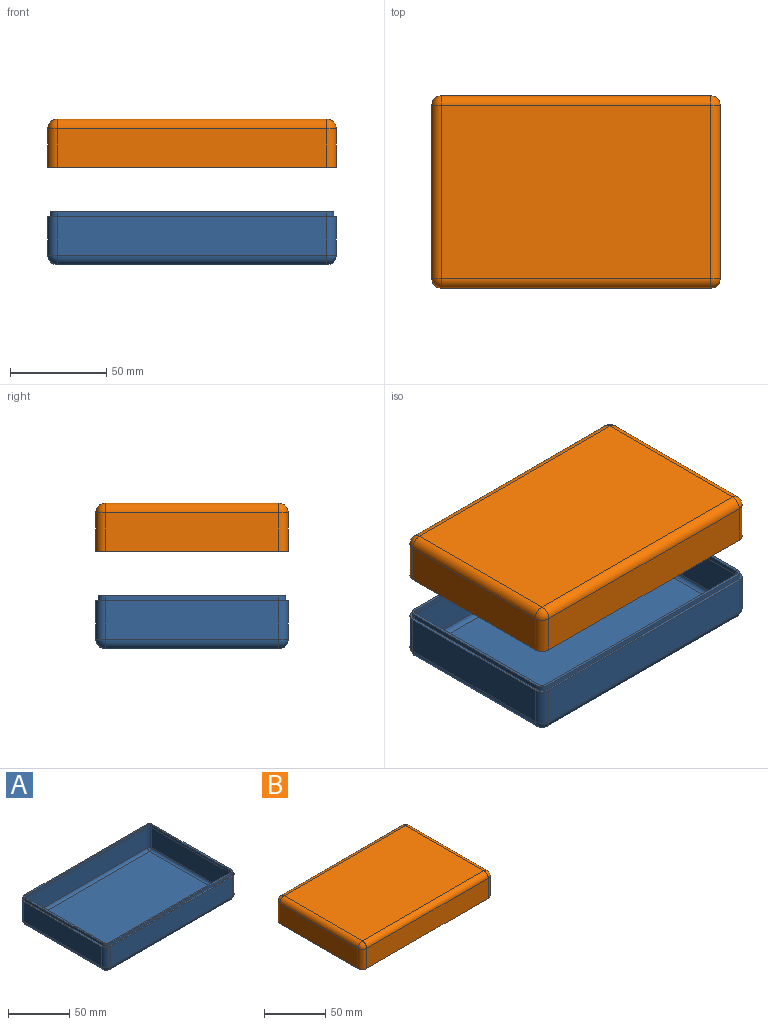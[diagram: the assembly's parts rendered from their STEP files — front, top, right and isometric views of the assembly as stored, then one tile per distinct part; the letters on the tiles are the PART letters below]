
ASSEMBLY  parts=2 mates=1
PART A: 53 faces, bbox 150x100x27.5 mm
  f0: plane 150x100mm, normal (0,0,1), area 624.4mm2, adj f10,f11,f12,f13,f14,f15,f16,f17
  f1: plane 140x90mm, normal (0,0,-1), area 12600mm2, adj f2,f3,f4,f5
  f2: cylinder r=5mm len=140mm, axis (1,0,0), area 1099.6mm2, adj f1,f8,f9,f17
  f3: cylinder r=5mm len=90mm, axis (0,1,0), area 706.9mm2, adj f1,f7,f9,f16
  f4: cylinder r=5mm len=140mm, axis (-1,0,0), area 1099.6mm2, adj f1,f6,f7,f14
  f5: cylinder r=5mm len=90mm, axis (0,-1,0), area 706.9mm2, adj f1,f6,f8,f12
  f6: sphere r=5mm, area 39.3mm2, adj f4,f5,f10
  f7: sphere r=5mm, area 39.3mm2, adj f3,f4,f13
  f8: sphere r=5mm, area 39.3mm2, adj f2,f5,f11
  f9: sphere r=5mm, area 39.3mm2, adj f2,f3,f15
  f10: cylinder r=5mm len=20mm, axis (0,0,1), area 157.1mm2, adj f0,f6,f12,f14
  f11: cylinder r=5mm len=20mm, axis (0,0,-1), area 157.1mm2, adj f0,f8,f12,f17
  f12: plane 90x20mm, normal (-1,0,0), area 1800mm2, adj f0,f5,f10,f11
  f13: cylinder r=5mm len=20mm, axis (0,0,-1), area 157.1mm2, adj f0,f7,f14,f16
  f14: plane 140x20mm, normal (0,1,0), area 2800mm2, adj f0,f4,f10,f13
  f15: cylinder r=5mm len=20mm, axis (0,0,1), area 157.1mm2, adj f0,f9,f16,f17
  f16: plane 90x20mm, normal (1,0,0), area 1800mm2, adj f0,f3,f13,f15
  f17: plane 140x20mm, normal (0,-1,0), area 2800mm2, adj f0,f2,f11,f15
  f18: cylinder r=3.72mm len=3.72mm, axis (0,0,-1), area 14.6mm2, adj f0,f20,f32,f33
  f19: cylinder r=2.47mm len=2.5mm, axis (0,0,-1), area 9.7mm2, adj f21,f32,f34,f35
  f20: plane 90x2.5mm, normal (-1,0,0), area 225mm2, adj f0,f18,f22,f32
  f21: plane 90x2.5mm, normal (1,0,0), area 225mm2, adj f19,f23,f32,f34
  f22: cylinder r=3.72mm len=3.72mm, axis (0,0,-1), area 14.6mm2, adj f0,f20,f24,f32
  f23: cylinder r=2.47mm len=2.5mm, axis (0,0,-1), area 9.7mm2, adj f21,f25,f32,f34
  f24: plane 140x2.5mm, normal (0,-1,0), area 350mm2, adj f0,f22,f26,f32
  f25: plane 140x2.5mm, normal (0,1,0), area 350mm2, adj f23,f27,f32,f34
  f26: cylinder r=3.72mm len=3.72mm, axis (0,0,-1), area 14.6mm2, adj f0,f24,f28,f32
  f27: cylinder r=2.47mm len=2.5mm, axis (0,0,-1), area 9.7mm2, adj f25,f29,f32,f34
  f28: plane 90x2.5mm, normal (1,0,0), area 225mm2, adj f0,f26,f30,f32
  f29: plane 90x2.5mm, normal (-1,0,0), area 225mm2, adj f27,f31,f32,f34
  f30: cylinder r=3.72mm len=3.72mm, axis (0,0,-1), area 14.6mm2, adj f0,f28,f32,f33
  f31: cylinder r=2.47mm len=2.5mm, axis (0,0,-1), area 9.7mm2, adj f29,f32,f34,f35
  f32: plane 147.44x97.44mm, normal (0,0,1), area 599.3mm2, adj f18,f19,f20,f21,f22,f23,f24,f25
  f33: plane 140x2.5mm, normal (0,1,0), area 350mm2, adj f0,f18,f30,f32
  f34: plane 145x95mm, normal (0,0,-1), area 14.8mm2, adj f19,f21,f23,f25,f27,f29,f31,f35
  f35: plane 140x2.5mm, normal (0,-1,0), area 350mm2, adj f19,f31,f32,f34
  f36: plane 140x90mm, normal (0,0,1), area 12600mm2, adj f37,f39,f41,f43
  f37: cylinder r=2.5mm len=90mm, axis (0,-1,0), area 353.4mm2, adj f36,f38,f44,f52
  f38: sphere r=2.5mm, area 9.8mm2, adj f37,f39,f51
  f39: cylinder r=2.5mm len=140mm, axis (-1,0,0), area 549.8mm2, adj f36,f38,f40,f50
  f40: sphere r=2.5mm, area 9.8mm2, adj f39,f41,f49
  f41: cylinder r=2.5mm len=90mm, axis (0,1,0), area 353.4mm2, adj f36,f40,f42,f48
  f42: sphere r=2.5mm, area 9.8mm2, adj f41,f43,f47
  f43: cylinder r=2.5mm len=140mm, axis (1,0,0), area 549.8mm2, adj f36,f42,f44,f46
  f44: sphere r=2.5mm, area 9.8mm2, adj f37,f43,f45
  f45: cylinder r=2.5mm len=20mm, axis (0,0,-1), area 78.5mm2, adj f34,f44,f46,f52
  f46: plane 140x20mm, normal (0,1,0), area 2800mm2, adj f34,f43,f45,f47
  f47: cylinder r=2.5mm len=20mm, axis (0,0,1), area 78.5mm2, adj f34,f42,f46,f48
  f48: plane 90x20mm, normal (-1,0,0), area 1800mm2, adj f34,f41,f47,f49
  f49: cylinder r=2.5mm len=20mm, axis (0,0,-1), area 78.5mm2, adj f34,f40,f48,f50
  f50: plane 140x20mm, normal (0,-1,0), area 2800mm2, adj f34,f39,f49,f51
  f51: cylinder r=2.5mm len=20mm, axis (0,0,1), area 78.5mm2, adj f34,f38,f50,f52
  f52: plane 90x20mm, normal (1,0,0), area 1800mm2, adj f34,f37,f45,f51
PART B: 44 faces, bbox 150x100x25 mm
  f0: plane 150x100mm, normal (0,0,-1), area 624.4mm2, adj f1,f2,f3,f4,f6,f10,f11,f17
  f1: plane 140x20mm, normal (0,-1,0), area 2800mm2, adj f0,f11,f14,f17
  f2: plane 90x20mm, normal (1,0,0), area 1800mm2, adj f0,f10,f15,f17
  f3: plane 140x20mm, normal (0,1,0), area 2800mm2, adj f0,f6,f9,f10
  f4: plane 90x20mm, normal (-1,0,0), area 1800mm2, adj f0,f6,f8,f11
  f5: plane 140x90mm, normal (0,0,1), area 12600mm2, adj f8,f9,f14,f15
  f6: cylinder r=5mm len=20mm, axis (0,0,1), area 157.1mm2, adj f0,f3,f4,f7
  f7: sphere r=5mm, area 39.3mm2, adj f6,f8,f9
  f8: cylinder r=5mm len=90mm, axis (0,1,0), area 706.9mm2, adj f4,f5,f7,f12
  f9: cylinder r=5mm len=140mm, axis (1,0,0), area 1099.6mm2, adj f3,f5,f7,f13
  f10: cylinder r=5mm len=20mm, axis (0,0,-1), area 157.1mm2, adj f0,f2,f3,f13
  f11: cylinder r=5mm len=20mm, axis (0,0,-1), area 157.1mm2, adj f0,f1,f4,f12
  f12: sphere r=5mm, area 39.3mm2, adj f8,f11,f14
  f13: sphere r=5mm, area 39.3mm2, adj f9,f10,f15
  f14: cylinder r=5mm len=140mm, axis (-1,0,0), area 1099.6mm2, adj f1,f5,f12,f16
  f15: cylinder r=5mm len=90mm, axis (0,-1,0), area 706.9mm2, adj f2,f5,f13,f16
  f16: sphere r=5mm, area 39.3mm2, adj f14,f15,f17
  f17: cylinder r=5mm len=20mm, axis (0,0,1), area 157.1mm2, adj f0,f1,f2,f16
  f18: plane 147.44x97.44mm, normal (0,0,-1), area 584.5mm2, adj f19,f20,f21,f22,f23,f24,f25,f26
  f19: cylinder r=3.72mm len=3.72mm, axis (0,0,-1), area 14.6mm2, adj f0,f18,f20,f26
  f20: plane 90x2.5mm, normal (1,0,0), area 225mm2, adj f0,f18,f19,f21
  f21: cylinder r=3.72mm len=3.72mm, axis (0,0,-1), area 14.6mm2, adj f0,f18,f20,f22
  f22: plane 140x2.5mm, normal (0,1,0), area 350mm2, adj f0,f18,f21,f23
  f23: cylinder r=3.72mm len=3.72mm, axis (0,0,-1), area 14.6mm2, adj f0,f18,f22,f24
  f24: plane 90x2.5mm, normal (-1,0,0), area 225mm2, adj f0,f18,f23,f25
  f25: cylinder r=3.72mm len=3.72mm, axis (0,0,-1), area 14.6mm2, adj f0,f18,f24,f26
  f26: plane 140x2.5mm, normal (0,-1,0), area 350mm2, adj f0,f18,f19,f25
  f27: plane 140x90mm, normal (0,0,-1), area 12600mm2, adj f28,f29,f30,f31
  f28: cylinder r=2.5mm len=140mm, axis (-1,0,0), area 549.8mm2, adj f27,f34,f35,f43
  f29: cylinder r=2.5mm len=90mm, axis (0,-1,0), area 353.4mm2, adj f27,f33,f35,f42
  f30: cylinder r=2.5mm len=140mm, axis (1,0,0), area 549.8mm2, adj f27,f32,f33,f40
  f31: cylinder r=2.5mm len=90mm, axis (0,1,0), area 353.4mm2, adj f27,f32,f34,f38
  f32: sphere r=2.5mm, area 9.8mm2, adj f30,f31,f36
  f33: sphere r=2.5mm, area 9.8mm2, adj f29,f30,f39
  f34: sphere r=2.5mm, area 9.8mm2, adj f28,f31,f37
  f35: sphere r=2.5mm, area 9.8mm2, adj f28,f29,f41
  f36: cylinder r=2.5mm len=17.5mm, axis (0,0,1), area 68.7mm2, adj f18,f32,f38,f40
  f37: cylinder r=2.5mm len=17.5mm, axis (0,0,-1), area 68.7mm2, adj f18,f34,f38,f43
  f38: plane 90x17.5mm, normal (1,0,0), area 1575mm2, adj f18,f31,f36,f37
  f39: cylinder r=2.5mm len=17.5mm, axis (0,0,-1), area 68.7mm2, adj f18,f33,f40,f42
  f40: plane 140x17.5mm, normal (0,-1,0), area 2450mm2, adj f18,f30,f36,f39
  f41: cylinder r=2.5mm len=17.5mm, axis (0,0,1), area 68.7mm2, adj f18,f35,f42,f43
  f42: plane 90x17.5mm, normal (-1,0,0), area 1575mm2, adj f18,f29,f39,f41
  f43: plane 140x17.5mm, normal (0,1,0), area 2450mm2, adj f18,f28,f37,f41
PLACE A t=(13.17,-4.77,-18.3)mm
PLACE B t=(13.17,-4.77,7.41)mm
MATE slider B.f27 <-> A.f36  axis (0,0,-1) through (13.17,-4.77,29.91)mm
